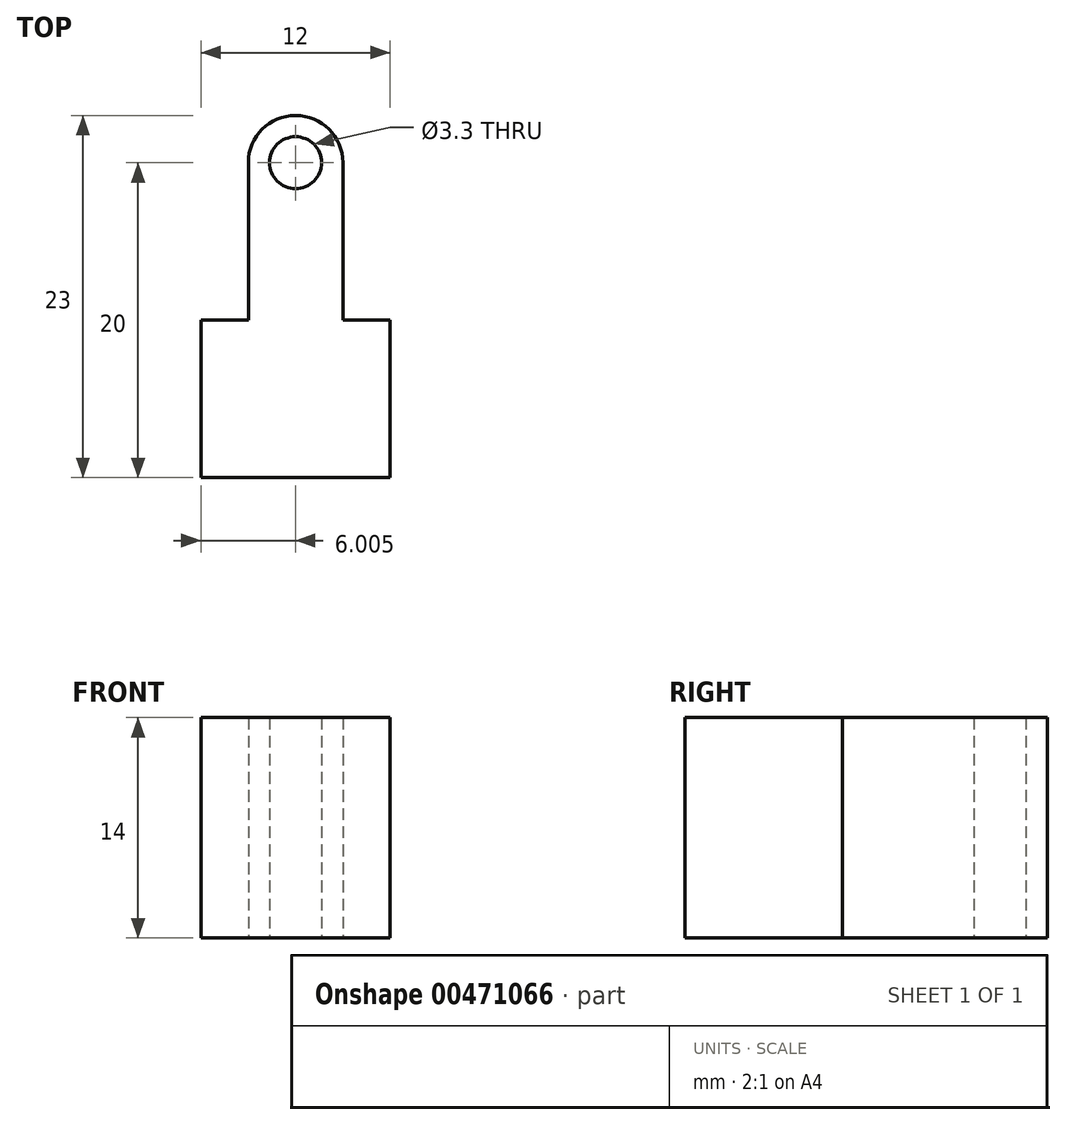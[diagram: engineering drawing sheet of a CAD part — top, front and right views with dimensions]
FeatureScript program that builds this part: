
annotation { "Feature Type Name" : "Feature", "Feature Type Description" : "" }
export const myFeature = defineFeature(function(context is Context, id is Id, definition is map)
    precondition{}
    {
        {
            var Q0;
            Q0=qCreatedBy(makeId("Top.planeOp"),FACE);
            var sketch = newSketch(context, id + "F0", { "sketchPlane" : qUnion([Q0])});
            skLineSegment(sketch, "E0", {"start": v(-39.96, -4.1) * mm, "end": v(-39.96, -14.1) * mm});
            skLineSegment(sketch, "E1", {"start": v(-39.96, -14.1) * mm, "end": v(-27.96, -14.1) * mm});
            skLineSegment(sketch, "E2", {"start": v(-27.96, -14.1) * mm, "end": v(-27.96, -4.1) * mm});
            skLineSegment(sketch, "E3", {"start": v(-27.96, -4.1) * mm, "end": v(-30.96, -4.1) * mm});
            skLineSegment(sketch, "E4", {"start": v(-30.96, -4.1) * mm, "end": v(-30.96, 5.9) * mm});
            skLineSegment(sketch, "E5", {"start": v(-39.96, -4.1) * mm, "end": v(-36.96, -4.1) * mm});
            skLineSegment(sketch, "E6", {"start": v(-36.96, -4.1) * mm, "end": v(-36.96, 5.9) * mm});
            skArc(sketch, "E7", {"start": v(-30.96, 5.9) * mm, "mid": v(-33.96, 8.9) * mm, "end": v(-36.96, 5.9) * mm});
            skCircle(sketch, "E8", {"center": v(-33.96, 5.9) * mm, "radius": 1.65 * mm});
            skSolve(sketch);
        }
        {
            var Q0;
            Q0 = qSketchRegion(id + "F0", true);
            extrude(context, id + "F1", {"entities" : qUnion([Q0]), "depth" : 14 * mm, "offsetDistance" : 25 * mm});
        }
    });
